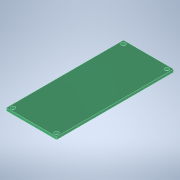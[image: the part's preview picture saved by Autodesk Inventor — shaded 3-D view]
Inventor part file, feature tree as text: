
AUTODESK INVENTOR PART (.ipt)
format: ipt  version: 2021 (Build 250183000, 183)  size: 125,952 bytes
history: native  units: mm
features: extrude x2, sketch x2, other x1
ambient origin geometry x8: Origin, YZ Plane, XZ Plane, XY Plane, X Axis, Y Axis, Z Axis, Center Point
bodies: Volumenkörper1 (feature_tree), Volumenkörper2 (feature_tree)
feature tree (5):
  extrude  "Extrusion1"  Depth=30.0mm
  extrude  "Extrusion2"  Depth=10.0mm
  other  "Kombinieren1"
  sketch  "Skizze1"  dims[d0=70.0mm d1=30.0mm]
  sketch  "Skizze2"  dims[d2=1.6mm d3=0.0mm d4=13.0mm d5=33.0mm d6=2.5mm d7=33.0mm d8=13.0mm d9=33.0mm d10=33.0mm d11=13.0mm d12=13.0mm d13=2.5mm d14=2.5mm d15=2.5mm d16=10.0mm d17=0.0mm]
